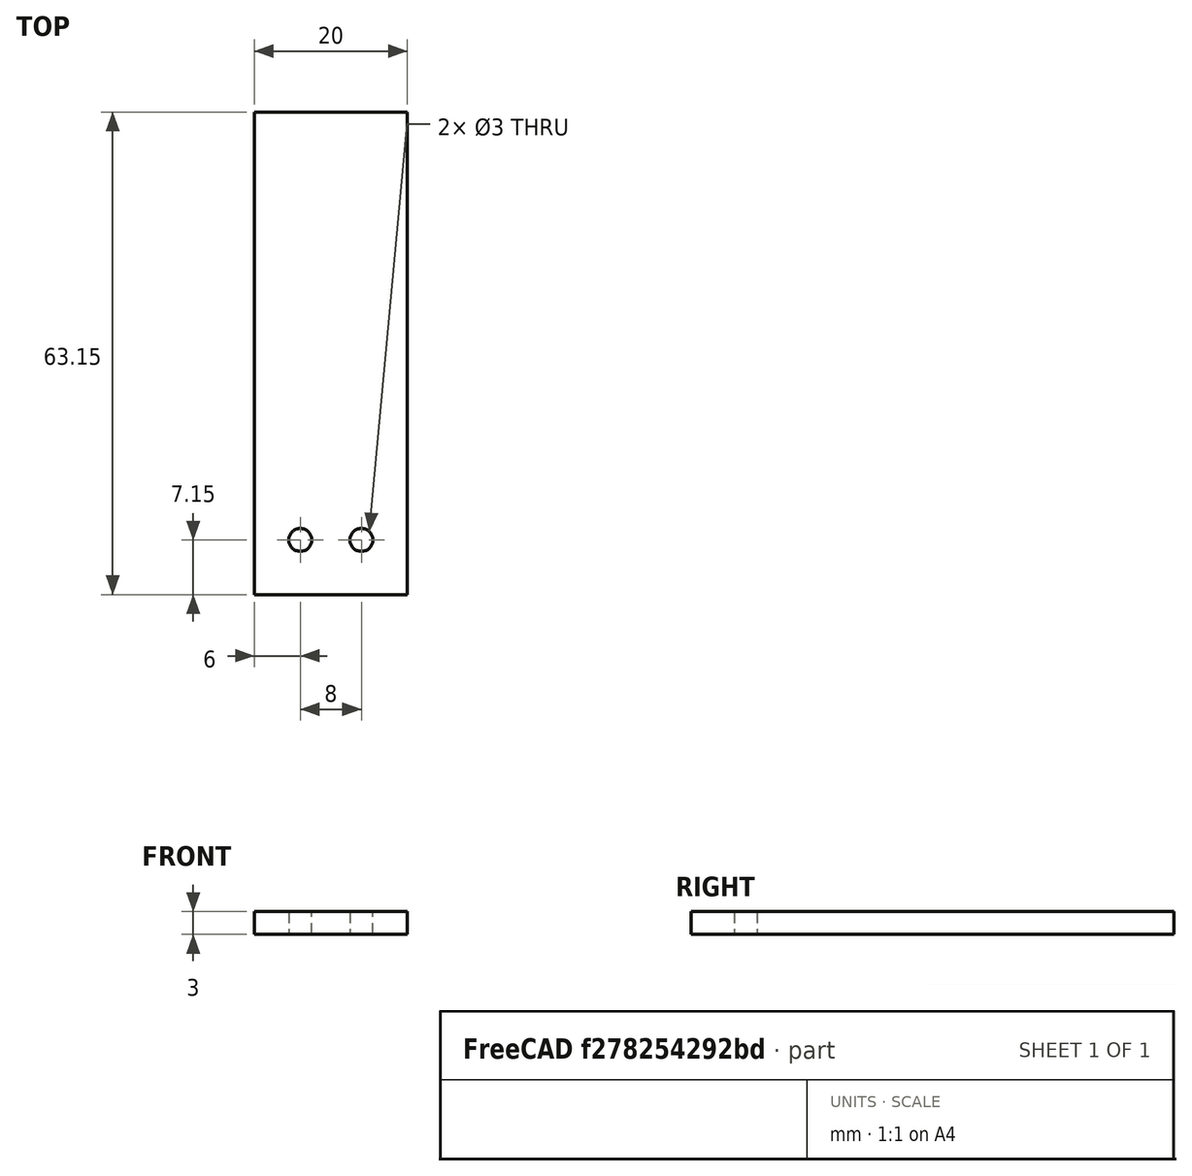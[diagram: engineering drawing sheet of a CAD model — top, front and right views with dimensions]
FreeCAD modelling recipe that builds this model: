
FCSTD DOCUMENT  (FreeCAD 0.16R6707 (Git))
Label: butée
License: All rights reserved
LicenseURL: http://en.wikipedia.org/wiki/All_rights_reserved
objects: Sketcher::SketchObject×1, PartDesign::Pad×1, Drawing::FeatureViewPart×1, Drawing::FeaturePage×1
note: 3 computed .brp shape members not serialized (recipe doc carries the construction recipe); baked Part::Feature solids carry a one-line shape summary decoded from their .brp

FEATURE [Sketcher::SketchObject] Sketch
  sketch-geometry (8):
    g0: LineSegment StartX=0 StartY=0 StartZ=0 EndX=20 EndY=0 EndZ=0
    g1: LineSegment StartX=20 StartY=0 StartZ=0 EndX=20 EndY=63.15 EndZ=0
    g2: LineSegment StartX=20 StartY=63.15 StartZ=0 EndX=0 EndY=63.15 EndZ=0
    g3: LineSegment StartX=0 StartY=63.15 StartZ=0 EndX=0 EndY=0 EndZ=0
    g4: GeomPoint [constr] X=6 Y=7.15 Z=0
    g5: GeomPoint [constr] X=14 Y=7.15 Z=0
    g6: Circle CenterX=6 CenterY=7.15 CenterZ=0 NormalX=0 NormalY=0 NormalZ=1 Radius=1.5
    g7: Circle CenterX=14 CenterY=7.15 CenterZ=0 NormalX=0 NormalY=0 NormalZ=1 Radius=1.5
  constraints (19):
    c: Coincident(g0,g1)
    c: Coincident(g1,g2)
    c: Coincident(g2,g3)
    c: Coincident(g3,g0)
    c: Horizontal(g0)
    c: Horizontal(g2)
    c: Vertical(g1)
    c: Vertical(g3)
    c: Coincident(g0,g-1)
    c: DistanceY(g3,g3) = 63.15
    c: Distance(g2) = 20
    c: DistanceX(g4) = 6
    c: DistanceX(g5,g0) = 6
    c: DistanceY(g5,g4) = 0
    c: DistanceY(g-1,g4) = 7.15
    c: Coincident(g6,g4)
    c: Coincident(g7,g5)
    c: Radius(g6) = 1.5
    c: Equal(g6,g7)
FEATURE [PartDesign::Pad] Pad
  Length = 3
  Length2 = 100
  Sketch = -> Sketch
  Type = 0
FEATURE [Drawing::FeatureViewPart] Ortho  label="Ortho_0_0"
  Direction = (0,0,1)
  HiddenWidth = 0.15
  LineWidth = 0.35
  Rotation = 0
  ShowHiddenLines = false
  ShowSmoothLines = false
  Source = -> Pad
  Tolerance = 0.05
  ViewResult = <g id="Ortho_0_0"\n   transform="rotate(0,105,180.075) translate(105,180.075) scale(1,1)"\n  >\n<g   stroke="rgb(0, 0, 0)"\n   stroke-width="0.35"\n   stroke-linecap="butt"\n   stroke-linejoin="miter"\n   fill="none"\n   transform="scale(1,-1)"\n  >\n<path id= "1" d=" M 0 0 L 20 0 " />\n<path id= "2" d=" M 20 0 L 20 63.15 " />\n<path id= "3" d=" M 20 63.15 L 0 63.15 " />\n<path id= "4" d=" M 0 63.15 L 0 -7.10543e-15 " />\n<circle cx ="14" cy ="7.15" r ="1.5" /><circle cx ="6" cy ="7.15" r ="1.5" /></g>\n</g>
  Visible = true
  X = 105
  Y = 180.075
FEATURE [Drawing::FeaturePage] Page
  EditableTexts = AUTHOR NAME | CREATION DATE | SUPERVISOR NAME | CHECK DATE | SCALE | WEIGHT | NUMBER | SHEET | TITLE | SUBTITLE
  Group = -> [Ortho]
